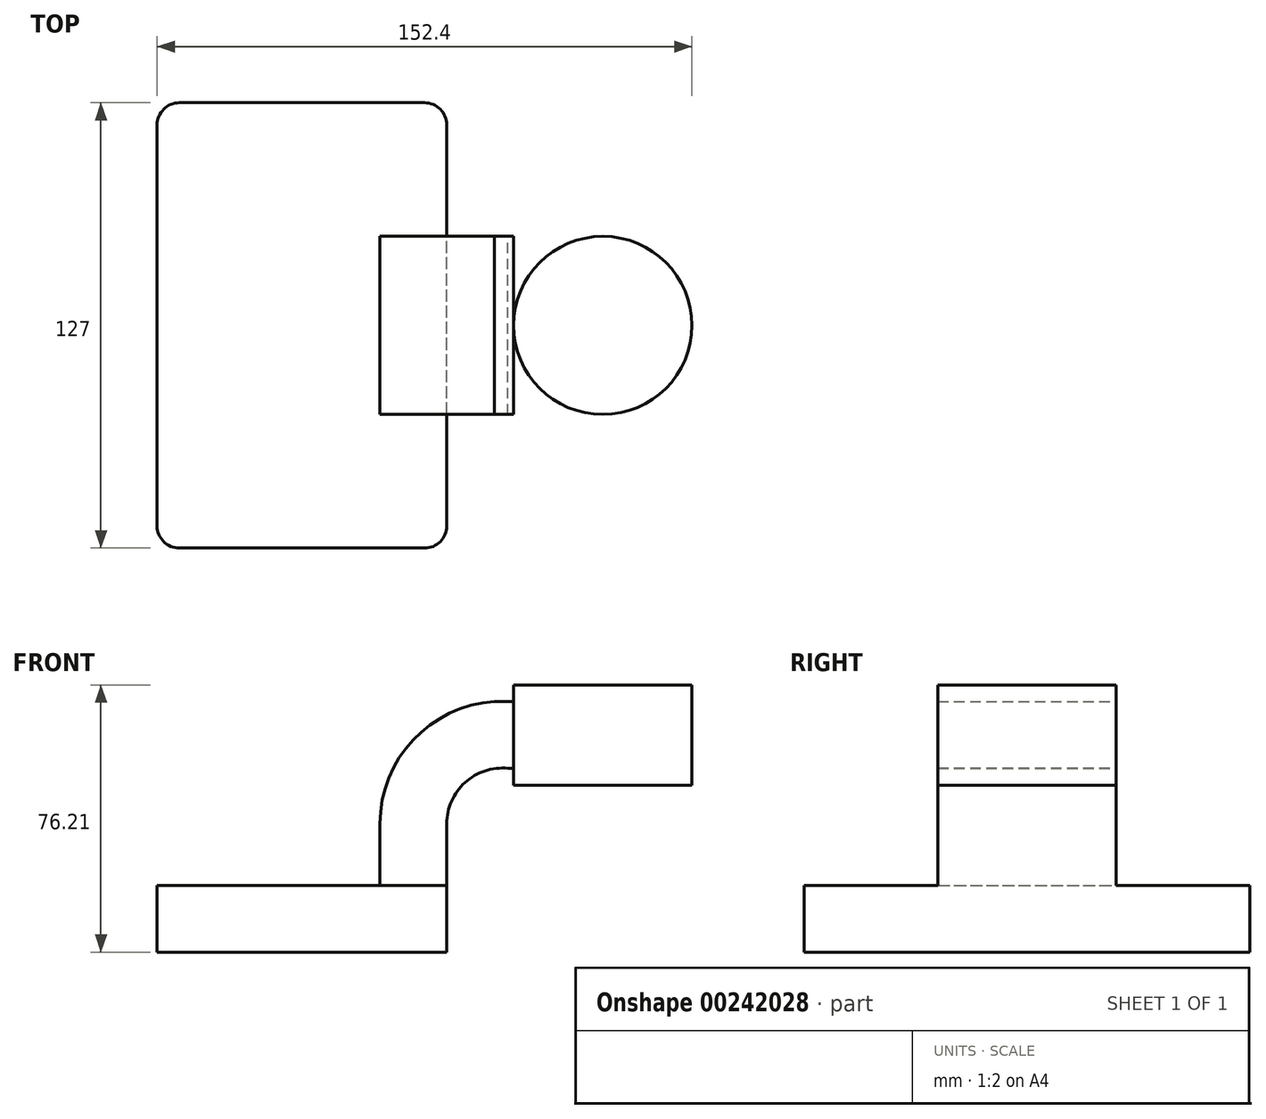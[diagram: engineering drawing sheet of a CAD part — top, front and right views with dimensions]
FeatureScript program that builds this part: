
annotation { "Feature Type Name" : "Feature", "Feature Type Description" : "" }
export const myFeature = defineFeature(function(context is Context, id is Id, definition is map)
    precondition{}
    {
        {
            var Q0;
            Q0=qCreatedBy(makeId("Front.planeOp"),FACE);
            var sketch = newSketch(context, id + "F0", { "sketchPlane" : qUnion([Q0])});
            skLineSegment(sketch, "E0.bottom", {"start": v(-41.28, 9.52) * mm, "end": v(41.27, 9.53) * mm});
            skLineSegment(sketch, "E0.top", {"start": v(-41.28, -9.52) * mm, "end": v(41.28, -9.52) * mm});
            skLineSegment(sketch, "E0.left", {"start": v(-41.28, 9.52) * mm, "end": v(-41.28, -9.53) * mm});
            skLineSegment(sketch, "E0.right", {"start": v(41.27, 9.53) * mm, "end": v(41.28, -9.52) * mm});
            skPoint(sketch, "E0.middle", {"position": v(0, 0) * mm});
            skLineSegment(sketch, "E1", {"start": v(41.27, 9.53) * mm, "end": v(41.27, 27.07) * mm});
            skArc(sketch, "E2", {"start": v(41.27, 27.07) * mm, "mid": v(46.48, 38.83) * mm, "end": v(58.67, 42.88) * mm});
            skLineSegment(sketch, "E3", {"start": v(58.67, 42.88) * mm, "end": v(85.73, 42.88) * mm});
            skLineSegment(sketch, "E4.bottom", {"start": v(111.12, 38.1) * mm, "end": v(60.32, 38.1) * mm});
            skLineSegment(sketch, "E4.top", {"start": v(111.12, 66.68) * mm, "end": v(60.32, 66.68) * mm});
            skLineSegment(sketch, "E4.left", {"start": v(111.12, 38.1) * mm, "end": v(111.12, 66.68) * mm});
            skLineSegment(sketch, "E4.right", {"start": v(60.32, 38.1) * mm, "end": v(60.32, 66.68) * mm});
            skPoint(sketch, "E4.middle", {"position": v(85.72, 52.39) * mm});
            skLineSegment(sketch, "E5.0", {"start": v(54.89, 61.93) * mm, "end": v(85.73, 61.93) * mm});
            skArc(sketch, "E5.1", {"start": v(22.23, 27.07) * mm, "mid": v(31.67, 50.96) * mm, "end": v(54.89, 61.93) * mm});
            skLineSegment(sketch, "E5.2", {"start": v(22.22, 9.53) * mm, "end": v(22.22, 27.07) * mm});
            skLineSegment(sketch, "E6", {"start": v(85.72, 38.1) * mm, "end": v(85.72, 66.68) * mm});
            skFitSpline(sketch, "E7", {"points": [v(-41.28, 9.52) * mm, v(54.89, 61.93) * mm], "startDerivative": vector(0, 61.34) * mm, "endDerivative": vector(129.88, 2.77) * mm});
            skSolve(sketch);
        }
        {
            var Q0;
            Q0=makeQuery(id+"F0.imprint","IMPRINT",FACE,{"disambiguationData":[TD([[makeQuery(id+"F0.imprint","IMPRINT",EDGE,{"derivedFrom":sQuery(id+"F0.wireOp",EDGE,"E0.top")}),1.0]])]});
            extrude(context, id + "F1", {"entities" : qUnion([Q0]), "endBound" : BoundingType.SYMMETRIC, "depth" : 127 * mm});
        }
        {
            var Q0;
            {var subQ7=sQuery(id+"F0.wireOp",EDGE,"E1");Q0=makeQuery(id+"F0.imprint","IMPRINT",FACE,{"disambiguationData":[TD([[makeQuery(id+"F0.imprint","IMPRINT",EDGE,{"derivedFrom":subQ7}),1.0]])]});}
            extrude(context, id + "F2", {"entities" : qUnion([Q0]), "operationType" : NewBodyOperationType.ADD, "endBound" : BoundingType.SYMMETRIC, "depth" : 50.8 * mm});
        }
        {
            var Q0;
            Q0=makeQuery(id+"F0.imprint","IMPRINT",FACE,{"disambiguationData":[TD([[makeQuery(id+"F0.imprint","IMPRINT",EDGE,{"derivedFrom":sQuery(id+"F0.wireOp",EDGE,"E5.1")}),1.0]])]});
            extrude(context, id + "F3", {"entities" : qUnion([Q0]), "operationType" : NewBodyOperationType.ADD, "endBound" : BoundingType.SYMMETRIC, "depth" : 15.88 * mm});
        }
        {
            var Q0;
            {var subQ4=sQuery(id+"F0.wireOp",EDGE,"E4.left");Q0=makeQuery(id+"F0.imprint","IMPRINT",FACE,{"disambiguationData":[TD([[makeQuery(id+"F0.imprint","IMPRINT",EDGE,{"derivedFrom":subQ4}),1.0]])]});}
            var Q1;
            Q1=sQuery(id+"F0.wireOp",EDGE,"E6");
            revolve(context, id + "F4", {"operationType" : NewBodyOperationType.ADD, "entities" : qUnion([Q0]), "axis" : qUnion([Q1]), "revolveType" : RevolveType.FULL});
        }
        {
            var Q0;
            Q0=makeQuery(id+"F1.opExtrude","CAP_EDGE",EDGE,{"disambiguationData":[OSD([sQuery(id+"F0.wireOp",EDGE,"E0.right")])],"isStart":false});
            fillet(context, id + "F5", {"entities" : qUnion([Q0]), "radius" : 6.35 * mm, "tangentPropagation" : true, "allowEdgeOverflow" : false});
        }
        {
            var Q0;
            Q0=makeQuery(id+"F1.opExtrude","CAP_EDGE",EDGE,{"disambiguationData":[OSD([sQuery(id+"F0.wireOp",EDGE,"E0.left")])],"isStart":false});
            var Q1;
            Q1=makeQuery(id+"F1.opExtrude","CAP_EDGE",EDGE,{"disambiguationData":[OSD([sQuery(id+"F0.wireOp",EDGE,"E0.right")])],"isStart":true});
            var Q2;
            Q2=makeQuery(id+"F1.opExtrude","CAP_EDGE",EDGE,{"disambiguationData":[OSD([sQuery(id+"F0.wireOp",EDGE,"E0.left")])],"isStart":true});
            fillet(context, id + "F6", {"entities" : qUnion([Q0, Q1, Q2]), "radius" : 6.35 * mm, "tangentPropagation" : true, "allowEdgeOverflow" : false});
        }
    });
